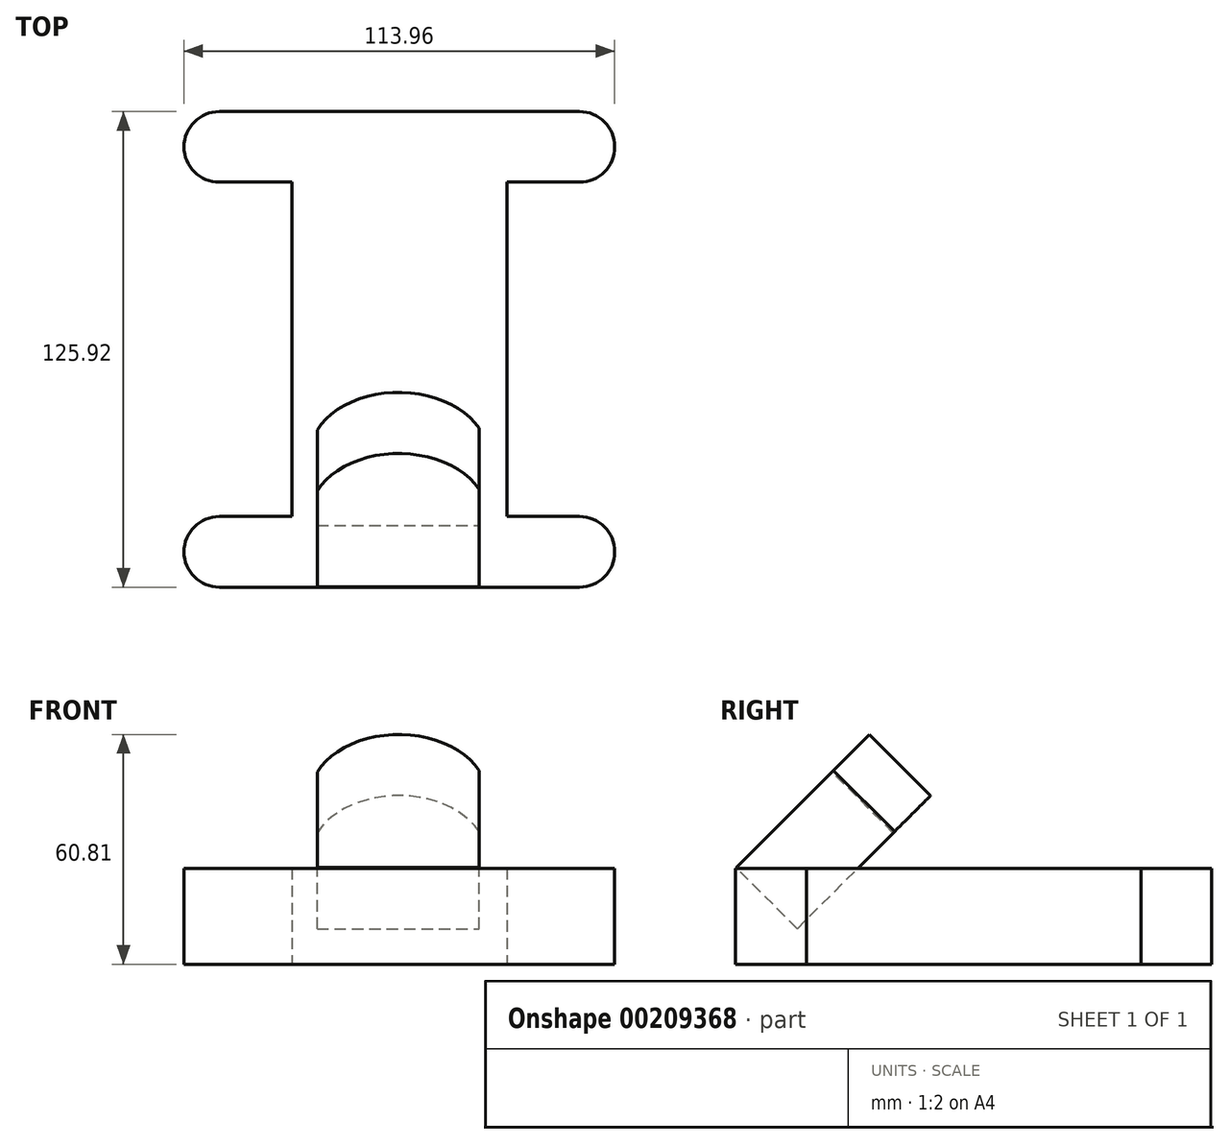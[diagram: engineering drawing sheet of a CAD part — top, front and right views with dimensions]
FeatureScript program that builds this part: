
annotation { "Feature Type Name" : "Feature", "Feature Type Description" : "" }
export const myFeature = defineFeature(function(context is Context, id is Id, definition is map)
    precondition{}
    {
        {
            var Q0;
            Q0=qCreatedBy(makeId("Top.planeOp"),FACE);
            var sketch = newSketch(context, id + "F0", { "sketchPlane" : qUnion([Q0])});
            skLineSegment(sketch, "E0.bottom", {"start": v(47.63, -62.96) * mm, "end": v(-47.63, -62.96) * mm});
            skLineSegment(sketch, "E0.top", {"start": v(47.63, 62.96) * mm, "end": v(-47.63, 62.96) * mm});
            skPoint(sketch, "E0.middle", {"position": v(0, 0) * mm});
            skLineSegment(sketch, "E1.bottom", {"start": v(47.63, -44.26) * mm, "end": v(-47.63, -44.26) * mm});
            skLineSegment(sketch, "E1.top", {"start": v(47.63, 44.26) * mm, "end": v(-47.63, 44.26) * mm});
            skLineSegment(sketch, "E2.bottom", {"start": v(28.48, -44.26) * mm, "end": v(-28.48, -44.26) * mm});
            skLineSegment(sketch, "E2.top", {"start": v(28.48, 44.26) * mm, "end": v(-28.48, 44.26) * mm});
            skLineSegment(sketch, "E2.left", {"start": v(28.48, -44.26) * mm, "end": v(28.48, 44.26) * mm});
            skLineSegment(sketch, "E2.right", {"start": v(-28.48, -44.26) * mm, "end": v(-28.48, 44.26) * mm});
            skArc(sketch, "E3", {"start": v(47.63, 44.26) * mm, "mid": v(56.98, 53.6) * mm, "end": v(47.63, 62.96) * mm});
            skArc(sketch, "E4", {"start": v(47.63, -62.96) * mm, "mid": v(56.98, -53.6) * mm, "end": v(47.63, -44.26) * mm});
            skArc(sketch, "E5", {"start": v(-47.63, 62.96) * mm, "mid": v(-56.98, 53.6) * mm, "end": v(-47.63, 44.26) * mm});
            skArc(sketch, "E6", {"start": v(-47.63, -44.26) * mm, "mid": v(-56.98, -53.6) * mm, "end": v(-47.63, -62.96) * mm});
            skLineSegment(sketch, "E7", {"start": v(-28.48, -44.26) * mm, "end": v(-28.48, -62.96) * mm});
            skLineSegment(sketch, "E8", {"start": v(28.48, -44.26) * mm, "end": v(28.48, -62.96) * mm});
            skLineSegment(sketch, "E9", {"start": v(-28.48, 44.26) * mm, "end": v(-28.48, 62.96) * mm});
            skLineSegment(sketch, "E10", {"start": v(28.48, 44.26) * mm, "end": v(28.48, 62.96) * mm});
            skSolve(sketch);
        }
        {
            var Q0;
            Q0 = qSketchRegion(id + "F0", true);
            extrude(context, id + "F1", {"entities" : qUnion([Q0]), "depth" : 25.4 * mm});
        }
        {
            var Q0;
            Q0=makeQuery(id+"F1.opExtrude","CAP_EDGE",EDGE,{"disambiguationData":[OSD([sQuery(id+"F0.wireOp",EDGE,"E0.bottom")])],"isStart":false});
            cPlane(context, id + "F2", {"entities" : qUnion([Q0]), "cplaneType" : CPlaneType.LINE_ANGLE, "offset" : 0.03 * yard, "angle" : 45 * degree, "width" : 0.17 * yard, "height" : 0.17 * yard});
        }
        {
            var Q0;
            Q0=qCreatedBy(id+"F2.planeOp",FACE);
            var sketch = newSketch(context, id + "F3", { "sketchPlane" : qUnion([Q0])});
            skLineSegment(sketch, "E11", {"start": v(-21.74, -26.35) * mm, "end": v(21.09, -26.35) * mm});
            skLineSegment(sketch, "E12", {"start": v(21.09, -26.35) * mm, "end": v(21.09, 10.1) * mm});
            skLineSegment(sketch, "E13", {"start": v(-21.74, -26.35) * mm, "end": v(-21.74, 9.52) * mm});
            skArc(sketch, "E14", {"start": v(21.09, 10.1) * mm, "mid": v(-0.5, 23.5) * mm, "end": v(-21.74, 9.52) * mm});
            skSolve(sketch);
        }
        {
            var Q0;
            Q0 = qSketchRegion(id + "F3", true);
            extrude(context, id + "F4", {"entities" : qUnion([Q0]), "oppositeDirection" : true, "depth" : 0.03 * yard});
        }
    });
